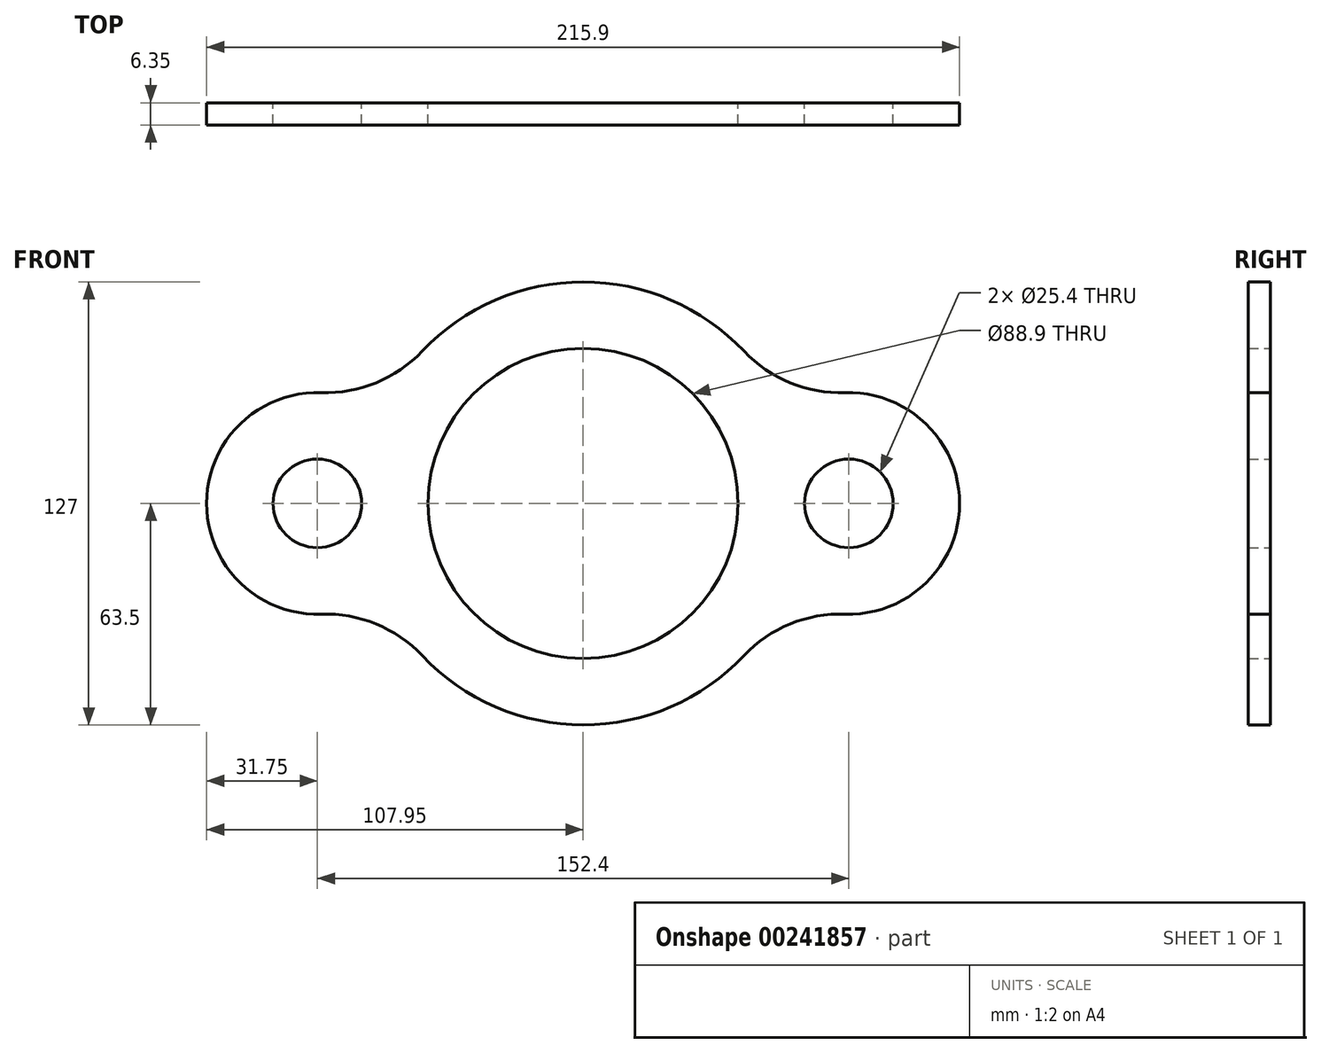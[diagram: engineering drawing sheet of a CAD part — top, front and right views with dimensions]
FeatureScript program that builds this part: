
annotation { "Feature Type Name" : "Feature", "Feature Type Description" : "" }
export const myFeature = defineFeature(function(context is Context, id is Id, definition is map)
    precondition{}
    {
        {
            var Q0;
            Q0=qCreatedBy(makeId("Front.planeOp"),FACE);
            var sketch = newSketch(context, id + "F0", { "sketchPlane" : qUnion([Q0])});
            skCircle(sketch, "E0", {"center": v(0, 0) * mm, "radius": 44.45 * mm});
            skCircle(sketch, "E1", {"center": v(76.2, 0) * mm, "radius": 12.7 * mm});
            skCircle(sketch, "E2", {"center": v(-76.2, 0) * mm, "radius": 12.7 * mm});
            skArc(sketch, "E3", {"start": v(-46.14, -43.63) * mm, "mid": v(0, -63.5) * mm, "end": v(46.14, -43.63) * mm});
            skArc(sketch, "E4", {"start": v(-75.12, 31.73) * mm, "mid": v(-107.95, 0) * mm, "end": v(-75.12, -31.73) * mm});
            skArc(sketch, "E5", {"start": v(75.12, -31.73) * mm, "mid": v(107.95, 0) * mm, "end": v(75.12, 31.73) * mm});
            skArc(sketch, "E6.trimOffspring", {"start": v(46.14, 43.63) * mm, "mid": v(0, 63.5) * mm, "end": v(-46.14, 43.63) * mm});
            skPoint(sketch, "E7.visualSharp", {"position": v(-57.94, 25.98) * mm});
            skArc(sketch, "E7.filletArc", {"start": v(-75.12, 31.73) * mm, "mid": v(-59.35, 34.56) * mm, "end": v(-46.14, 43.63) * mm});
            skPoint(sketch, "E8.visualSharp", {"position": v(57.94, 25.98) * mm});
            skArc(sketch, "E8.filletArc", {"start": v(46.14, 43.63) * mm, "mid": v(59.35, 34.56) * mm, "end": v(75.12, 31.73) * mm});
            skPoint(sketch, "E9.visualSharp", {"position": v(-57.94, -25.98) * mm});
            skArc(sketch, "E9.filletArc", {"start": v(-46.14, -43.63) * mm, "mid": v(-59.35, -34.56) * mm, "end": v(-75.12, -31.73) * mm});
            skPoint(sketch, "E10.visualSharp", {"position": v(57.94, -25.98) * mm});
            skArc(sketch, "E10.filletArc", {"start": v(75.12, -31.73) * mm, "mid": v(59.35, -34.56) * mm, "end": v(46.14, -43.63) * mm});
            skSolve(sketch);
        }
        {
            var Q0;
            Q0=makeQuery(id+"F0.imprint","IMPRINT",FACE,{"disambiguationData":[TD([[makeQuery(id+"F0.imprint","IMPRINT",EDGE,{"derivedFrom":sQuery(id+"F0.wireOp",EDGE,"E0")}),-1.0]])]});
            extrude(context, id + "F1", {"entities" : qUnion([Q0]), "depth" : 6.35 * mm});
        }
    });
